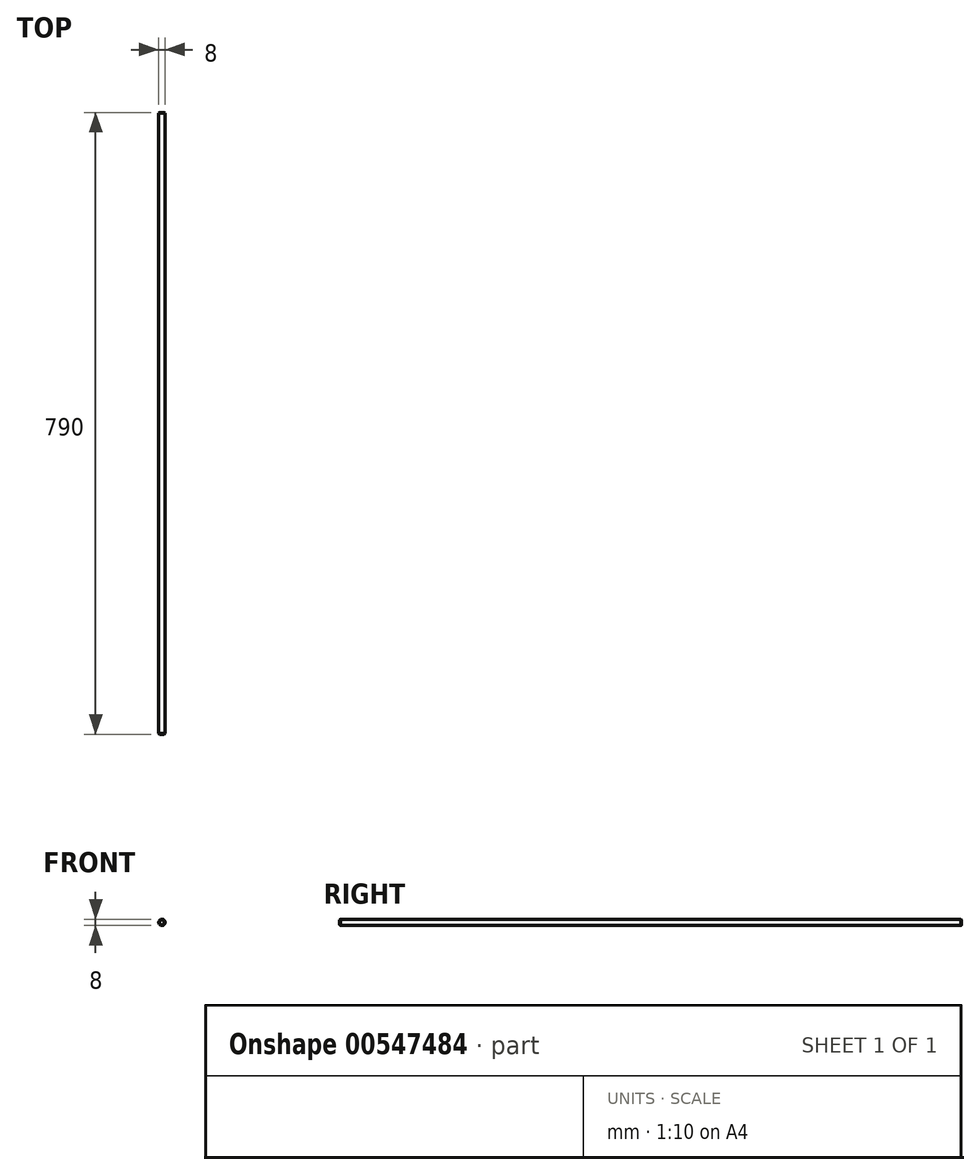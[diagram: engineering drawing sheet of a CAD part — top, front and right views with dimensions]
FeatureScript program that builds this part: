
annotation { "Feature Type Name" : "Feature", "Feature Type Description" : "" }
export const myFeature = defineFeature(function(context is Context, id is Id, definition is map)
    precondition{}
    {
        {
            var Q0;
            Q0=qCreatedBy(makeId("Front.planeOp"),FACE);
            var sketch = newSketch(context, id + "F0", { "sketchPlane" : qUnion([Q0])});
            skCircle(sketch, "E0", {"center": v(0, 0) * mm, "radius": 4 * mm});
            skSolve(sketch);
        }
        {
            var Q0;
            Q0 = qSketchRegion(id + "F0", true);
            extrude(context, id + "F1", {"entities" : qUnion([Q0]), "oppositeDirection" : true, "depth" : 790 * mm, "offsetDistance" : 25 * mm});
        }
        {
            var Q0;
            Q0=makeQuery(id+"F1.opExtrude","CAP_EDGE",EDGE,{"disambiguationData":[OSD([sQuery(id+"F0.wireOp",EDGE,"E0")])],"isStart":true});
            var Q1;
            Q1=makeQuery(id+"F1.opExtrude","CAP_FACE",FACE,{"disambiguationData":[OSD([sQuery(id+"F0.wireOp",EDGE,"E0")])],"isStart":false});
            chamfer(context, id + "F2", {"entities" : qUnion([Q0, Q1]), "width" : 1 * mm, "tangentPropagation" : true});
        }
    });
